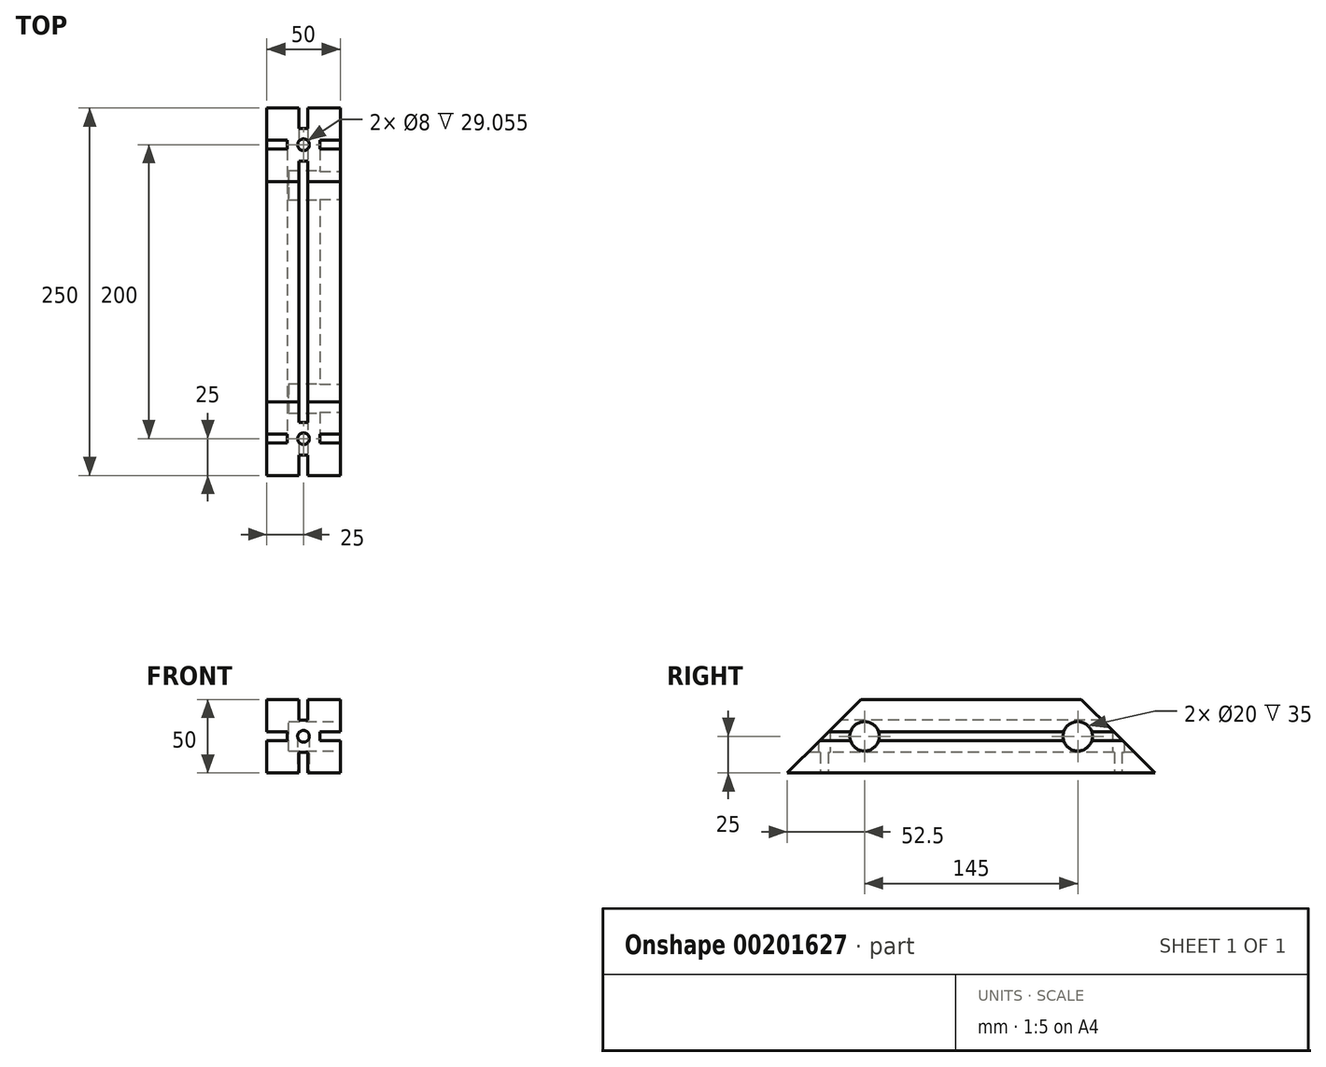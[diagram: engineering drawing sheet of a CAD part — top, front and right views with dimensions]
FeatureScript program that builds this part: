
annotation { "Feature Type Name" : "Feature", "Feature Type Description" : "" }
export const myFeature = defineFeature(function(context is Context, id is Id, definition is map)
    precondition{}
    {
        {
            var Q0;
            Q0=qCreatedBy(makeId("Front.planeOp"),FACE);
            var sketch = newSketch(context, id + "F0", { "sketchPlane" : qUnion([Q0])});
            skLineSegment(sketch, "E0.bottom", {"start": v(25, -25) * mm, "end": v(-25, -25) * mm});
            skLineSegment(sketch, "E0.top", {"start": v(25, 25) * mm, "end": v(-25, 25) * mm});
            skLineSegment(sketch, "E0.left", {"start": v(25, -25) * mm, "end": v(25, 25) * mm});
            skLineSegment(sketch, "E0.right", {"start": v(-25, -25) * mm, "end": v(-25, 25) * mm});
            skPoint(sketch, "E0.middle", {"position": v(0, 0) * mm});
            skSolve(sketch);
        }
        {
            var Q0;
            Q0=qSketchRegion(id+"F0",true);
            extrude(context, id + "F1", {"entities" : qUnion([Q0]), "offsetDistance" : 25 * mm, "depth" : 250 * mm});
        }
        {
            var Q0;
            Q0=makeQuery(id+"F1.opExtrude","SWEPT_FACE",FACE,{"disambiguationData":[OSD([sQuery(id+"F0.wireOp",EDGE,"E0.left")])]});
            var sketch = newSketch(context, id + "F2", { "sketchPlane" : qUnion([Q0])});
            skLineSegment(sketch, "E1", {"start": v(-640.44, 0) * mm, "end": v(-250, 0) * mm, "construction": true});
            skCircle(sketch, "E2", {"center": v(-825, 50) * mm, "radius": 4 * mm});
            skCircle(sketch, "E3.1.0.0", {"center": v(-625, 50) * mm, "radius": 4 * mm});
            skCircle(sketch, "E3.2.0.0", {"center": v(-425, 50) * mm, "radius": 4 * mm});
            skCircle(sketch, "E3.3.0.0", {"center": v(-225, 50) * mm, "radius": 4 * mm});
            skCircle(sketch, "E3.4.0.0", {"center": v(-25, 50) * mm, "radius": 4 * mm});
            skLineSegment(sketch, "E3.direction1", {"start": v(-825, 50) * mm, "end": v(-625, 50) * mm, "construction": true});
            skCircle(sketch, "E4.0.5.0", {"center": v(175, 50) * mm, "radius": 4 * mm});
            skCircle(sketch, "E4.0.6.0", {"center": v(375, 50) * mm, "radius": 4 * mm});
            skCircle(sketch, "E4.0.7.0", {"center": v(575, 50) * mm, "radius": 4 * mm});
            skCircle(sketch, "E5.MirrorC", {"center": v(-625, -50) * mm, "radius": 4 * mm});
            skCircle(sketch, "E6.MirrorC", {"center": v(-425, -50) * mm, "radius": 4 * mm});
            skCircle(sketch, "E7.MirrorC", {"center": v(-225, -50) * mm, "radius": 4 * mm});
            skCircle(sketch, "E8.MirrorC", {"center": v(575, -50) * mm, "radius": 4 * mm});
            skCircle(sketch, "E9.MirrorC", {"center": v(375, -50) * mm, "radius": 4 * mm});
            skCircle(sketch, "E10.MirrorC", {"center": v(-25, -50) * mm, "radius": 4 * mm});
            skCircle(sketch, "E11.MirrorC", {"center": v(175, -50) * mm, "radius": 4 * mm});
            skCircle(sketch, "E12.MirrorC", {"center": v(-825, -50) * mm, "radius": 4 * mm});
            skCircle(sketch, "E13", {"center": v(-825, 0) * mm, "radius": 4 * mm});
            skCircle(sketch, "E14.1.0.0", {"center": v(-625, 0) * mm, "radius": 4 * mm});
            skCircle(sketch, "E14.2.0.0", {"center": v(-425, 0) * mm, "radius": 4 * mm});
            skLineSegment(sketch, "E14.direction1", {"start": v(-825, 0) * mm, "end": v(-625, 0) * mm, "construction": true});
            skCircle(sketch, "E15.0.3.0", {"center": v(-225, 0) * mm, "radius": 4 * mm});
            skCircle(sketch, "E15.0.4.0", {"center": v(-25, 0) * mm, "radius": 4 * mm});
            skCircle(sketch, "E15.0.5.0", {"center": v(175, 0) * mm, "radius": 4 * mm});
            skCircle(sketch, "E15.0.6.0", {"center": v(375, 0) * mm, "radius": 4 * mm});
            skCircle(sketch, "E15.0.7.0", {"center": v(575, 0) * mm, "radius": 4 * mm});
            skLineSegment(sketch, "E16", {"start": v(-225, 50) * mm, "end": v(-25, 50) * mm, "construction": true});
            skLineSegment(sketch, "E17", {"start": v(-125, 50) * mm, "end": v(-125, -25) * mm, "construction": true});
            skLineSegment(sketch, "E18", {"start": v(-825, 50) * mm, "end": v(-825, 0) * mm, "construction": true});
            skSolve(sketch);
        }
        {
            var Q0;
            Q0=makeQuery(id+"F1.opExtrude","SWEPT_FACE",FACE,{"disambiguationData":[OSD([sQuery(id+"F0.wireOp",EDGE,"E0.bottom")])]});
            var sketch = newSketch(context, id + "F3", { "sketchPlane" : qUnion([Q0])});
            skLineSegment(sketch, "E19", {"start": v(0, 1392.8) * mm, "end": v(0, 250) * mm, "construction": true});
            skCircle(sketch, "E20", {"center": v(0, 825) * mm, "radius": 4 * mm});
            skCircle(sketch, "E21.0.1.0", {"center": v(0, 625) * mm, "radius": 4 * mm});
            skCircle(sketch, "E21.0.2.0", {"center": v(0, 425) * mm, "radius": 4 * mm});
            skCircle(sketch, "E21.0.3.0", {"center": v(0, 225) * mm, "radius": 4 * mm});
            skCircle(sketch, "E21.0.4.0", {"center": v(0, 25) * mm, "radius": 4 * mm});
            skCircle(sketch, "E21.0.5.0", {"center": v(0, -175) * mm, "radius": 4 * mm});
            skCircle(sketch, "E21.0.6.0", {"center": v(0, -375) * mm, "radius": 4 * mm});
            skCircle(sketch, "E21.0.7.0", {"center": v(0, -575) * mm, "radius": 4 * mm});
            skLineSegment(sketch, "E21.direction1", {"start": v(0, 825) * mm, "end": v(25, 825) * mm, "construction": true});
            skLineSegment(sketch, "E21.direction2", {"start": v(0, 825) * mm, "end": v(0, 625) * mm, "construction": true});
            skLineSegment(sketch, "E22", {"start": v(0, 225) * mm, "end": v(0, 25) * mm, "construction": true});
            skLineSegment(sketch, "E23", {"start": v(0, 125) * mm, "end": v(25, 125) * mm, "construction": true});
            skPoint(sketch, "E23.endSnap0", {"position": v(0, 125) * mm});
            skSolve(sketch);
        }
        {
            var Q0;
            Q0=qSketchRegion(id+"F3",true);
            extrude(context, id + "F4", {"entities" : qUnion([Q0]), "operationType" : NewBodyOperationType.REMOVE, "endBound" : BoundingType.THROUGH_ALL, "oppositeDirection" : true, "depth" : 25 * mm});
        }
        {
            var Q0;
            Q0=makeQuery(id+"F1.opExtrude","CAP_FACE",FACE,{"disambiguationData":[OSD([sQuery(id+"F0.wireOp",EDGE,"E0.bottom"),sQuery(id+"F0.wireOp",EDGE,"E0.top"),sQuery(id+"F0.wireOp",EDGE,"E0.left"),sQuery(id+"F0.wireOp",EDGE,"E0.right")])],"isStart":false});
            var sketch = newSketch(context, id + "F5", { "sketchPlane" : qUnion([Q0])});
            skLineSegment(sketch, "E24", {"start": v(0, 25) * mm, "end": v(0, -25) * mm, "construction": true});
            skLineSegment(sketch, "E25", {"start": v(-25, 50) * mm, "end": v(25, 50) * mm, "construction": true});
            skLineSegment(sketch, "E26.bottom", {"start": v(3, 11) * mm, "end": v(-3, 11) * mm});
            skLineSegment(sketch, "E26.top", {"start": v(3, 25) * mm, "end": v(-3, 25) * mm});
            skLineSegment(sketch, "E26.left", {"start": v(3, 11) * mm, "end": v(3, 25) * mm});
            skLineSegment(sketch, "E26.right", {"start": v(-3, 11) * mm, "end": v(-3, 25) * mm});
            skPoint(sketch, "E26.middle", {"position": v(0, 18) * mm});
            skLineSegment(sketch, "E27", {"start": v(-25, 0) * mm, "end": v(25, 0) * mm, "construction": true});
            skLineSegment(sketch, "E28.MirrorCS", {"start": v(-3, -11) * mm, "end": v(-3, -25) * mm});
            skLineSegment(sketch, "E29.MirrorCS", {"start": v(3, -25) * mm, "end": v(-3, -25) * mm});
            skLineSegment(sketch, "E30.MirrorCS", {"start": v(3, -11) * mm, "end": v(3, -25) * mm});
            skLineSegment(sketch, "E31.MirrorCS", {"start": v(3, -11) * mm, "end": v(-3, -11) * mm});
            skLineSegment(sketch, "E32.bottom", {"start": v(-25, 47) * mm, "end": v(-11, 47) * mm});
            skLineSegment(sketch, "E32.top", {"start": v(-25, 53) * mm, "end": v(-11, 53) * mm});
            skLineSegment(sketch, "E32.left", {"start": v(-25, 47) * mm, "end": v(-25, 53) * mm});
            skLineSegment(sketch, "E32.right", {"start": v(-11, 47) * mm, "end": v(-11, 53) * mm});
            skPoint(sketch, "E32.middle", {"position": v(-18, 50) * mm});
            skLineSegment(sketch, "E33.bottom", {"start": v(-25, -3) * mm, "end": v(-11, -3) * mm});
            skLineSegment(sketch, "E33.top", {"start": v(-25, 3) * mm, "end": v(-11, 3) * mm});
            skLineSegment(sketch, "E33.left", {"start": v(-25, -3) * mm, "end": v(-25, 3) * mm});
            skLineSegment(sketch, "E33.right", {"start": v(-11, -3) * mm, "end": v(-11, 3) * mm});
            skPoint(sketch, "E33.middle", {"position": v(-18, 0) * mm});
            skLineSegment(sketch, "E34.MirrorCS", {"start": v(-25, -47) * mm, "end": v(-11, -47) * mm});
            skLineSegment(sketch, "E35.MirrorCS", {"start": v(-25, -53) * mm, "end": v(-11, -53) * mm});
            skLineSegment(sketch, "E36.MirrorCS", {"start": v(-11, -47) * mm, "end": v(-11, -53) * mm});
            skLineSegment(sketch, "E37.MirrorCS", {"start": v(-25, -47) * mm, "end": v(-25, -53) * mm});
            skLineSegment(sketch, "E38.MirrorCS", {"start": v(25, 47) * mm, "end": v(11, 47) * mm});
            skLineSegment(sketch, "E39.MirrorCS", {"start": v(25, 53) * mm, "end": v(11, 53) * mm});
            skLineSegment(sketch, "E40.MirrorCS", {"start": v(11, 47) * mm, "end": v(11, 53) * mm});
            skLineSegment(sketch, "E41.MirrorCS", {"start": v(25, 47) * mm, "end": v(25, 53) * mm});
            skLineSegment(sketch, "E42.MirrorCS", {"start": v(25, -3) * mm, "end": v(11, -3) * mm});
            skLineSegment(sketch, "E43.MirrorCS", {"start": v(25, 3) * mm, "end": v(11, 3) * mm});
            skLineSegment(sketch, "E44.MirrorCS", {"start": v(11, -3) * mm, "end": v(11, 3) * mm});
            skLineSegment(sketch, "E45.MirrorCS", {"start": v(25, -3) * mm, "end": v(25, 3) * mm});
            skLineSegment(sketch, "E46.MirrorCS", {"start": v(25, -47) * mm, "end": v(11, -47) * mm});
            skLineSegment(sketch, "E47.MirrorCS", {"start": v(25, -53) * mm, "end": v(11, -53) * mm});
            skLineSegment(sketch, "E48.MirrorCS", {"start": v(11, -47) * mm, "end": v(11, -53) * mm});
            skLineSegment(sketch, "E49.MirrorCS", {"start": v(25, -47) * mm, "end": v(25, -53) * mm});
            skSolve(sketch);
        }
        {
            var Q0;
            Q0=qSketchRegion(id+"F5",true);
            extrude(context, id + "F6", {"entities" : qUnion([Q0]), "operationType" : NewBodyOperationType.REMOVE, "endBound" : BoundingType.THROUGH_ALL, "oppositeDirection" : true, "depth" : 25 * mm});
        }
        {
            var Q0;
            Q0=makeQuery(id+"F1.opExtrude","SWEPT_FACE",FACE,{"disambiguationData":[OSD([sQuery(id+"F0.wireOp",EDGE,"E0.right")])]});
            var sketch = newSketch(context, id + "F7", { "sketchPlane" : qUnion([Q0])});
            skLineSegment(sketch, "E50", {"start": v(0, 25) * mm, "end": v(50, 25) * mm});
            skLineSegment(sketch, "E51", {"start": v(50, 25) * mm, "end": v(0, -25) * mm});
            skLineSegment(sketch, "E52", {"start": v(125, 25) * mm, "end": v(125, -25) * mm, "construction": true});
            skLineSegment(sketch, "E53.MirrorCS", {"start": v(200, 25) * mm, "end": v(250, -25) * mm});
            skLineSegment(sketch, "E54.MirrorCS", {"start": v(250, 25) * mm, "end": v(200, 25) * mm});
            skLineSegment(sketch, "E55", {"start": v(0, 25) * mm, "end": v(0, -25) * mm});
            skLineSegment(sketch, "E56.MirrorCS", {"start": v(250, 25) * mm, "end": v(250, -25) * mm});
            skSolve(sketch);
        }
        {
            var Q0;
            Q0 = qSketchRegion(id + "F7", true);
            extrude(context, id + "F8", {"entities" : qUnion([Q0]), "operationType" : NewBodyOperationType.REMOVE, "endBound" : BoundingType.THROUGH_ALL, "oppositeDirection" : true, "depth" : 25 * mm});
        }
        {
            var Q0;
            {var subQ1=sQuery(id+"F0.wireOp",EDGE,"E0.left");var subQ2=sQuery(id+"F0.wireOp",EDGE,"E0.top");Q0=makeQuery(id+"F6.boolean.opBoolean","SPLIT",FACE,{"disambiguationData":[TD([makeQuery(id+"F1.opExtrude","SWEPT_FACE",FACE,{"disambiguationData":[OSD([subQ2])]})])],"derivedFrom":makeQuery(id+"F1.opExtrude","SWEPT_FACE",FACE,{"disambiguationData":[OSD([subQ1])]})});}
            var sketch = newSketch(context, id + "F9", { "sketchPlane" : qUnion([Q0])});
            skLineSegment(sketch, "E57", {"start": v(-125, 25) * mm, "end": v(-125, 71.58) * mm, "construction": true});
            skCircle(sketch, "E58", {"center": v(-197.5, 0) * mm, "radius": 10 * mm});
            skCircle(sketch, "E59.MirrorC", {"center": v(-52.5, 0) * mm, "radius": 10 * mm});
            skSolve(sketch);
        }
        {
            var Q0;
            Q0 = qSketchRegion(id + "F9", true);
            extrude(context, id + "F10", {"entities" : qUnion([Q0]), "operationType" : NewBodyOperationType.REMOVE, "oppositeDirection" : true, "depth" : 35 * mm, "offsetDistance" : 25 * mm});
        }
    });
